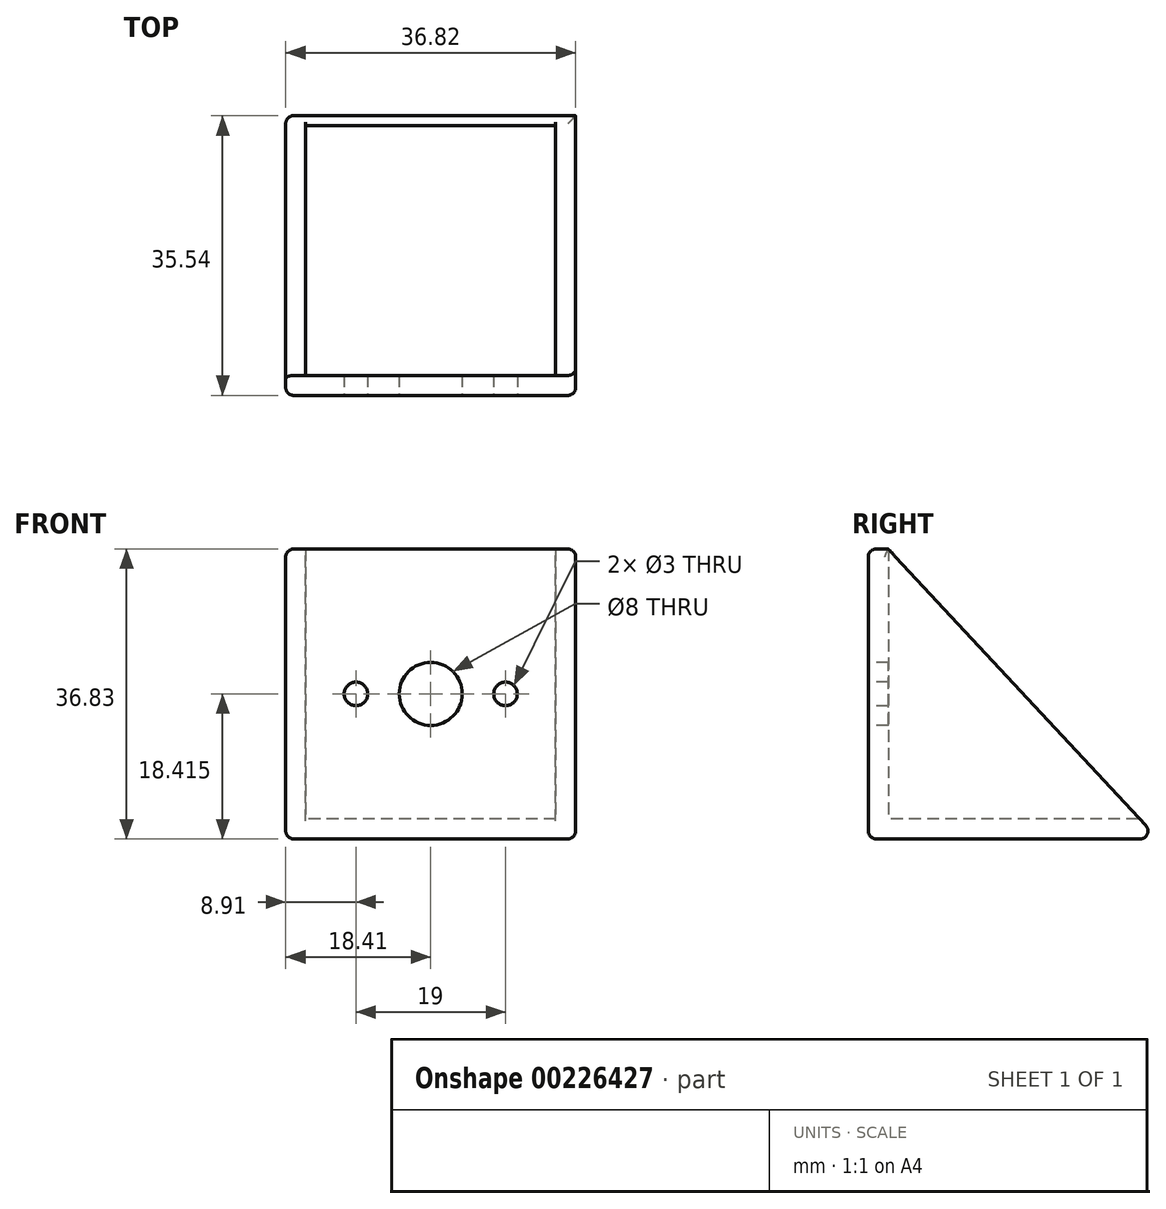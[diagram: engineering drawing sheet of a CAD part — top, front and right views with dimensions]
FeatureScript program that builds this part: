
annotation { "Feature Type Name" : "Feature", "Feature Type Description" : "" }
export const myFeature = defineFeature(function(context is Context, id is Id, definition is map)
    precondition{}
    {
        {
            var Q0;
            Q0=qCreatedBy(makeId("Top.planeOp"),FACE);
            var sketch = newSketch(context, id + "F0", { "sketchPlane" : qUnion([Q0])});
            skLineSegment(sketch, "E0.bottom", {"start": v(15.88, 15.87) * mm, "end": v(-15.87, 15.87) * mm});
            skLineSegment(sketch, "E0.top", {"start": v(15.87, -15.88) * mm, "end": v(-15.87, -15.88) * mm});
            skLineSegment(sketch, "E0.left", {"start": v(15.87, 15.87) * mm, "end": v(15.87, -15.88) * mm});
            skLineSegment(sketch, "E0.right", {"start": v(-15.88, 15.87) * mm, "end": v(-15.87, -15.88) * mm});
            skPoint(sketch, "E0.middle", {"position": v(0, 0) * mm});
            skLineSegment(sketch, "E1.0", {"start": v(18.41, -18.41) * mm, "end": v(-18.41, -18.41) * mm});
            skLineSegment(sketch, "E1.1", {"start": v(18.41, 18.41) * mm, "end": v(18.41, -18.41) * mm});
            skLineSegment(sketch, "E1.2", {"start": v(18.41, 18.41) * mm, "end": v(-18.42, 18.41) * mm});
            skLineSegment(sketch, "E1.3", {"start": v(-18.42, 18.41) * mm, "end": v(-18.41, -18.41) * mm});
            skSolve(sketch);
        }
        {
            var Q0;
            Q0=makeQuery(id+"F0.imprint","IMPRINT",FACE,{"disambiguationData":[TD([[makeQuery(id+"F0.imprint","IMPRINT",EDGE,{"derivedFrom":sQuery(id+"F0.wireOp",EDGE,"E0.bottom")}),-1.0]])]});
            extrude(context, id + "F1", {"entities" : qUnion([Q0]), "depth" : 36.83 * mm, "offsetDistance" : 25.4 * mm});
        }
        {
            var Q0;
            Q0=makeQuery(id+"F0.imprint","IMPRINT",FACE,{"disambiguationData":[TD([[makeQuery(id+"F0.imprint","IMPRINT",EDGE,{"derivedFrom":sQuery(id+"F0.wireOp",EDGE,"E0.bottom")}),1.0]])]});
            extrude(context, id + "F2", {"entities" : qUnion([Q0]), "operationType" : NewBodyOperationType.ADD, "depth" : 2.54 * mm, "offsetDistance" : 25.4 * mm});
        }
        {
            var Q0;
            Q0=makeQuery(id+"F1.opExtrude","SWEPT_FACE",FACE,{"disambiguationData":[OSD([sQuery(id+"F0.wireOp",EDGE,"E1.1")])]});
            var sketch = newSketch(context, id + "F3", { "sketchPlane" : qUnion([Q0])});
            skLineSegment(sketch, "E2", {"start": v(18.41, 0) * mm, "end": v(-15.88, 36.83) * mm});
            skSolve(sketch);
        }
        {
            var Q0;
            {var subQ0=sQuery(id+"F3.wireOp",EDGE,"E2");Q0=makeQuery(id+"F3.imprint","IMPRINT",FACE,{"disambiguationData":[TD([[makeQuery(id+"F3.imprint","IMPRINT",EDGE,{"derivedFrom":subQ0}),-1.0]])]});}
            extrude(context, id + "F4", {"entities" : qUnion([Q0]), "operationType" : NewBodyOperationType.REMOVE, "endBound" : BoundingType.THROUGH_ALL, "oppositeDirection" : true, "depth" : 25.4 * mm, "offsetDistance" : 25.4 * mm});
        }
        {
            var Q0;
            Q0=makeQuery(id+"F1.opExtrude","SWEPT_FACE",FACE,{"disambiguationData":[OSD([sQuery(id+"F0.wireOp",EDGE,"E1.0")])]});
            var sketch = newSketch(context, id + "F5", { "sketchPlane" : qUnion([Q0])});
            skCircle(sketch, "E3", {"center": v(0, 18.41) * mm, "radius": 9.5 * mm, "construction": true});
            skPoint(sketch, "E3.centerSnap0", {"position": v(18.41, 18.41) * mm});
            skCircle(sketch, "E4", {"center": v(9.5, 18.41) * mm, "radius": 1.5 * mm});
            skCircle(sketch, "E5", {"center": v(-9.5, 18.41) * mm, "radius": 1.5 * mm});
            skCircle(sketch, "E6", {"center": v(0, 18.41) * mm, "radius": 4 * mm});
            skSolve(sketch);
        }
        {
            var Q0;
            Q0 = qSketchRegion(id + "F5", true);
            extrude(context, id + "F6", {"entities" : qUnion([Q0]), "operationType" : NewBodyOperationType.REMOVE, "oppositeDirection" : true, "depth" : 25.4 * mm, "offsetDistance" : 25.4 * mm});
        }
        {
            var Q0;
            {var subQ0=sQuery(id+"F0.wireOp",EDGE,"E0.left");var subQ2=sQuery(id+"F0.wireOp",EDGE,"E1.1");var subQ3=sQuery(id+"F3.wireOp",EDGE,"E2");Q0=makeQuery(id+"F4.boolean.opBoolean","COPY",EDGE,{"disambiguationData":[TD([makeQuery(id+"F1.opExtrude","SWEPT_FACE",FACE,{"disambiguationData":[OSD([subQ0])]})])],"derivedFrom":makeQuery(id+"F4.opExtrude","SWEPT_EDGE",EDGE,{"disambiguationData":[OSD([subQ2,subQ3])]})});}
            var Q1;
            Q1=makeQuery(id+"F1.opExtrude","CAP_EDGE",EDGE,{"disambiguationData":[OSD([sQuery(id+"F0.wireOp",EDGE,"E1.1")])],"isStart":false});
            var Q2;
            Q2=makeQuery(id+"F4.boolean.opBoolean","COPY",EDGE,{"derivedFrom":makeQuery(id+"F4.opExtrude","CAP_EDGE",EDGE,{"disambiguationData":[OSD([sQuery(id+"F3.wireOp",EDGE,"E2")])],"isStart":true})});
            var Q3;
            {var subQ0=sQuery(id+"F0.wireOp",EDGE,"E1.2");Q3=makeQuery(id+"F4.boolean.opBoolean","MERGE",EDGE,{"derivedFrom":[makeQuery(id+"F1.opExtrude","CAP_EDGE",EDGE,{"disambiguationData":[OSD([subQ0])],"isStart":true}),makeQuery(id+"F4.opExtrude","SWEPT_EDGE",EDGE,{"disambiguationData":[OSD([sQuery(id+"F0.wireOp",EDGE,"E1.1"),subQ0,sQuery(id+"F3.wireOp",EDGE,"E2")])]})]});}
            var Q4;
            Q4=makeQuery(id+"F4.boolean.opBoolean","INTERSECT",EDGE,{"derivedFrom":[makeQuery(id+"F1.opExtrude","SWEPT_FACE",FACE,{"disambiguationData":[OSD([sQuery(id+"F0.wireOp",EDGE,"E0.bottom")])]}),makeQuery(id+"F4.opExtrude","SWEPT_FACE",FACE,{"disambiguationData":[OSD([sQuery(id+"F3.wireOp",EDGE,"E2")])]})]});
            var Q5;
            Q5=makeQuery(id+"F4.boolean.opBoolean","INTERSECT",EDGE,{"derivedFrom":[makeQuery(id+"F1.opExtrude","SWEPT_FACE",FACE,{"disambiguationData":[OSD([sQuery(id+"F0.wireOp",EDGE,"E1.3")])]}),makeQuery(id+"F4.opExtrude","SWEPT_FACE",FACE,{"disambiguationData":[OSD([sQuery(id+"F3.wireOp",EDGE,"E2")])]})]});
            var Q6;
            Q6=makeQuery(id+"F1.opExtrude","CAP_EDGE",EDGE,{"disambiguationData":[OSD([sQuery(id+"F0.wireOp",EDGE,"E1.0")])],"isStart":false});
            var Q7;
            Q7=makeQuery(id+"F1.opExtrude","SWEPT_EDGE",EDGE,{"disambiguationData":[OSD([sQuery(id+"F0.wireOp",EDGE,"E1.0"),sQuery(id+"F0.wireOp",EDGE,"E1.3")])]});
            var Q8;
            Q8=makeQuery(id+"F1.opExtrude","SWEPT_EDGE",EDGE,{"disambiguationData":[OSD([sQuery(id+"F0.wireOp",EDGE,"E1.0"),sQuery(id+"F0.wireOp",EDGE,"E1.1")])]});
            var Q9;
            Q9=makeQuery(id+"F1.opExtrude","CAP_EDGE",EDGE,{"disambiguationData":[OSD([sQuery(id+"F0.wireOp",EDGE,"E1.3")])],"isStart":true});
            var Q10;
            Q10=makeQuery(id+"F1.opExtrude","CAP_EDGE",EDGE,{"disambiguationData":[OSD([sQuery(id+"F0.wireOp",EDGE,"E1.0")])],"isStart":true});
            var Q11;
            Q11=makeQuery(id+"F1.opExtrude","CAP_EDGE",EDGE,{"disambiguationData":[OSD([sQuery(id+"F0.wireOp",EDGE,"E1.1")])],"isStart":true});
            var Q12;
            Q12=makeQuery(id+"F1.opExtrude","CAP_EDGE",EDGE,{"disambiguationData":[OSD([sQuery(id+"F0.wireOp",EDGE,"E1.3")])],"isStart":false});
            fillet(context, id + "F7", {"entities" : qUnion([Q0, Q1, Q2, Q3, Q4, Q5, Q6, Q7, Q8, Q9, Q10, Q11, Q12]), "radius" : 1 * mm, "tangentPropagation" : true, "allowEdgeOverflow" : false});
        }
    });
